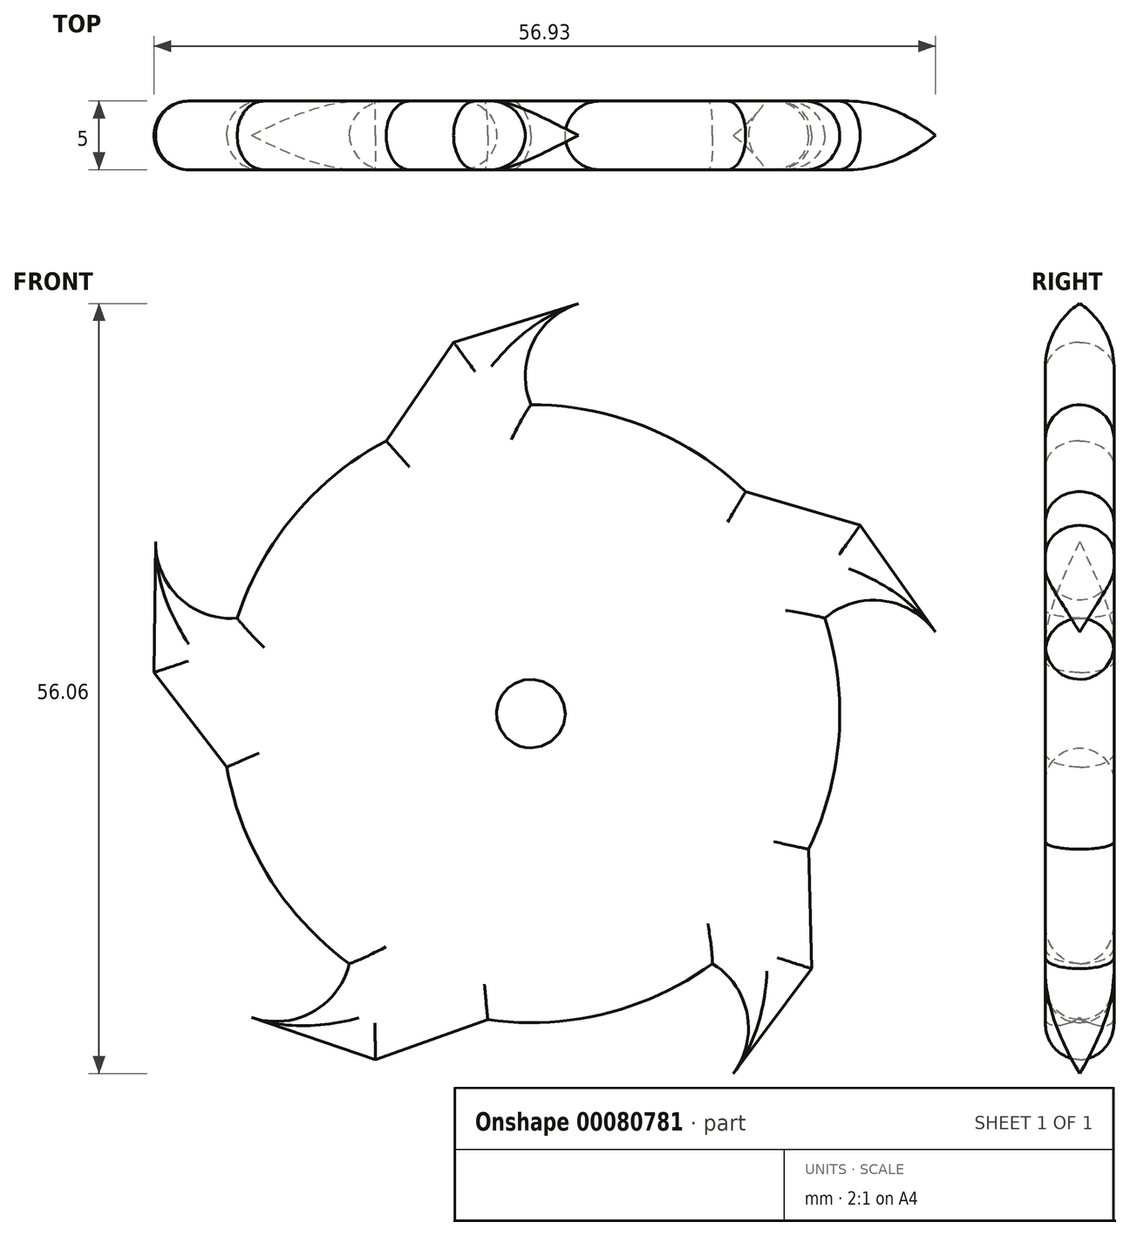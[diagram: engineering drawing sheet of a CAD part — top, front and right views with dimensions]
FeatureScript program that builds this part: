
annotation { "Feature Type Name" : "Feature", "Feature Type Description" : "" }
export const myFeature = defineFeature(function(context is Context, id is Id, definition is map)
    precondition{}
    {
        {
            var Q0;
            Q0=qCreatedBy(makeId("Front.planeOp"),FACE);
            var sketch = newSketch(context, id + "F0", { "sketchPlane" : qUnion([Q0])});
            skCircle(sketch, "E0", {"center": v(0, 0) * mm, "radius": 22.5 * mm});
            skLineSegment(sketch, "E1", {"start": v(-10.55, 19.87) * mm, "end": v(-5.64, 27.04) * mm});
            skLineSegment(sketch, "E2", {"start": v(-5.64, 27.04) * mm, "end": v(3.46, 29.86) * mm});
            skCircle(sketch, "E3", {"center": v(0, 0) * mm, "radius": 2.5 * mm});
            skArc(sketch, "E4", {"start": v(3.46, 29.86) * mm, "mid": v(0.1, 26.95) * mm, "end": v(0, 22.5) * mm});
            skLineSegment(sketch, "E5.1.0", {"start": v(-27.46, 3) * mm, "end": v(-27.33, 12.52) * mm});
            skLineSegment(sketch, "E5.1.1", {"start": v(-22.16, -3.9) * mm, "end": v(-27.46, 3) * mm});
            skArc(sketch, "E5.1.2", {"start": v(-27.33, 12.52) * mm, "mid": v(-25.6, 8.43) * mm, "end": v(-21.4, 6.95) * mm});
            skLineSegment(sketch, "E5.2.0", {"start": v(-11.34, -25.2) * mm, "end": v(-20.36, -22.13) * mm});
            skLineSegment(sketch, "E5.2.1", {"start": v(-3.14, -22.28) * mm, "end": v(-11.34, -25.2) * mm});
            skArc(sketch, "E5.2.2", {"start": v(-20.36, -22.13) * mm, "mid": v(-15.93, -21.74) * mm, "end": v(-13.23, -18.2) * mm});
            skLineSegment(sketch, "E6.1.3.0", {"start": v(20.46, -18.57) * mm, "end": v(14.75, -26.2) * mm});
            skLineSegment(sketch, "E6.3.3.0", {"start": v(20.22, -9.88) * mm, "end": v(20.46, -18.57) * mm});
            skArc(sketch, "E6.6.3.0", {"start": v(14.75, -26.2) * mm, "mid": v(15.75, -21.86) * mm, "end": v(13.23, -18.2) * mm});
            skLineSegment(sketch, "E6.1.4.0", {"start": v(23.98, 13.72) * mm, "end": v(29.47, 5.93) * mm});
            skLineSegment(sketch, "E6.3.4.0", {"start": v(15.64, 16.18) * mm, "end": v(23.98, 13.72) * mm});
            skArc(sketch, "E6.6.4.0", {"start": v(29.47, 5.93) * mm, "mid": v(25.66, 8.22) * mm, "end": v(21.4, 6.95) * mm});
            skSolve(sketch);
        }
        {
            var Q0;
            Q0=makeQuery(id+"F0.imprint","IMPRINT",FACE,{"disambiguationData":[TD([[makeQuery(id+"F0.imprint","IMPRINT",EDGE,{"derivedFrom":sQuery(id+"F0.wireOp",EDGE,"E3")}),-1.0]])]});
            var Q1;
            {var subQ0=sQuery(id+"F0.wireOp",EDGE,"E1");Q1=makeQuery(id+"F0.imprint","IMPRINT",FACE,{"disambiguationData":[TD([[makeQuery(id+"F0.imprint","IMPRINT",EDGE,{"derivedFrom":subQ0}),-1.0]])]});}
            var Q2;
            Q2=makeQuery(id+"F0.imprint","IMPRINT",FACE,{"disambiguationData":[TD([[makeQuery(id+"F0.imprint","IMPRINT",EDGE,{"derivedFrom":sQuery(id+"F0.wireOp",EDGE,"E5.1.0")}),-1.0]])]});
            var Q3;
            Q3=makeQuery(id+"F0.imprint","IMPRINT",FACE,{"disambiguationData":[TD([[makeQuery(id+"F0.imprint","IMPRINT",EDGE,{"derivedFrom":sQuery(id+"F0.wireOp",EDGE,"E5.2.0")}),-1.0]])]});
            var Q4;
            Q4=makeQuery(id+"F0.imprint","IMPRINT",FACE,{"disambiguationData":[TD([[makeQuery(id+"F0.imprint","IMPRINT",EDGE,{"derivedFrom":sQuery(id+"F0.wireOp",EDGE,"E6.1.3.0")}),-1.0]])]});
            var Q5;
            Q5=makeQuery(id+"F0.imprint","IMPRINT",FACE,{"disambiguationData":[TD([[makeQuery(id+"F0.imprint","IMPRINT",EDGE,{"derivedFrom":sQuery(id+"F0.wireOp",EDGE,"E6.1.4.0")}),-1.0]])]});
            var Q6;
            Q6=makeQuery(id+"F0.imprint","IMPRINT",FACE,{"disambiguationData":[TD([[makeQuery(id+"F0.imprint","IMPRINT",EDGE,{"derivedFrom":sQuery(id+"F0.wireOp",EDGE,"0a4afba6-e0dd-443b-8d0a-7748f586e94c.1.6.0")}),-1.0]])]});
            var Q7;
            Q7=makeQuery(id+"F0.imprint","IMPRINT",FACE,{"disambiguationData":[TD([[makeQuery(id+"F0.imprint","IMPRINT",EDGE,{"derivedFrom":sQuery(id+"F0.wireOp",EDGE,"0a4afba6-e0dd-443b-8d0a-7748f586e94c.1.5.0")}),-1.0]])]});
            extrude(context, id + "F1", {"entities" : qUnion([Q0, Q1, Q2, Q3, Q4, Q5, Q6, Q7]), "depth" : 5 * mm});
        }
        {
            var Q0;
            Q0=makeQuery(id+"F1.opExtrude","CAP_FACE",FACE,{"disambiguationData":[OSD([sQuery(id+"F0.wireOp",EDGE,"E0"),sQuery(id+"F0.wireOp",EDGE,"E1"),sQuery(id+"F0.wireOp",EDGE,"E2"),sQuery(id+"F0.wireOp",EDGE,"E3"),sQuery(id+"F0.wireOp",EDGE,"E4"),sQuery(id+"F0.wireOp",EDGE,"E5.1.0"),sQuery(id+"F0.wireOp",EDGE,"E5.1.1"),sQuery(id+"F0.wireOp",EDGE,"E5.1.2"),sQuery(id+"F0.wireOp",EDGE,"E5.2.0"),sQuery(id+"F0.wireOp",EDGE,"E5.2.1"),sQuery(id+"F0.wireOp",EDGE,"E5.2.2"),sQuery(id+"F0.wireOp",EDGE,"E6.1.3.0"),sQuery(id+"F0.wireOp",EDGE,"E6.3.3.0"),sQuery(id+"F0.wireOp",EDGE,"E6.6.3.0"),sQuery(id+"F0.wireOp",EDGE,"E6.1.4.0"),sQuery(id+"F0.wireOp",EDGE,"E6.3.4.0"),sQuery(id+"F0.wireOp",EDGE,"E6.6.4.0"),sQuery(id+"F0.wireOp",EDGE,"0a4afba6-e0dd-443b-8d0a-7748f586e94c.1.5.0"),sQuery(id+"F0.wireOp",EDGE,"0a4afba6-e0dd-443b-8d0a-7748f586e94c.3.5.0"),sQuery(id+"F0.wireOp",EDGE,"0a4afba6-e0dd-443b-8d0a-7748f586e94c.6.5.0"),sQuery(id+"F0.wireOp",EDGE,"0a4afba6-e0dd-443b-8d0a-7748f586e94c.1.6.0"),sQuery(id+"F0.wireOp",EDGE,"0a4afba6-e0dd-443b-8d0a-7748f586e94c.3.6.0"),sQuery(id+"F0.wireOp",EDGE,"0a4afba6-e0dd-443b-8d0a-7748f586e94c.6.6.0")])],"isStart":true});
            fillet(context, id + "F2", {"entities" : qUnion([Q0]), "radius" : 2.5 * mm, "tangentPropagation" : true, "allowEdgeOverflow" : false});
        }
        {
            var Q0;
            Q0=makeQuery(id+"F1.opExtrude","CAP_FACE",FACE,{"disambiguationData":[OSD([sQuery(id+"F0.wireOp",EDGE,"E0"),sQuery(id+"F0.wireOp",EDGE,"E1"),sQuery(id+"F0.wireOp",EDGE,"E2"),sQuery(id+"F0.wireOp",EDGE,"E3"),sQuery(id+"F0.wireOp",EDGE,"E4"),sQuery(id+"F0.wireOp",EDGE,"E5.1.0"),sQuery(id+"F0.wireOp",EDGE,"E5.1.1"),sQuery(id+"F0.wireOp",EDGE,"E5.1.2"),sQuery(id+"F0.wireOp",EDGE,"E5.2.0"),sQuery(id+"F0.wireOp",EDGE,"E5.2.1"),sQuery(id+"F0.wireOp",EDGE,"E5.2.2"),sQuery(id+"F0.wireOp",EDGE,"E6.1.3.0"),sQuery(id+"F0.wireOp",EDGE,"E6.3.3.0"),sQuery(id+"F0.wireOp",EDGE,"E6.6.3.0"),sQuery(id+"F0.wireOp",EDGE,"E6.1.4.0"),sQuery(id+"F0.wireOp",EDGE,"E6.3.4.0"),sQuery(id+"F0.wireOp",EDGE,"E6.6.4.0"),sQuery(id+"F0.wireOp",EDGE,"0a4afba6-e0dd-443b-8d0a-7748f586e94c.1.5.0"),sQuery(id+"F0.wireOp",EDGE,"0a4afba6-e0dd-443b-8d0a-7748f586e94c.3.5.0"),sQuery(id+"F0.wireOp",EDGE,"0a4afba6-e0dd-443b-8d0a-7748f586e94c.6.5.0"),sQuery(id+"F0.wireOp",EDGE,"0a4afba6-e0dd-443b-8d0a-7748f586e94c.1.6.0"),sQuery(id+"F0.wireOp",EDGE,"0a4afba6-e0dd-443b-8d0a-7748f586e94c.3.6.0"),sQuery(id+"F0.wireOp",EDGE,"0a4afba6-e0dd-443b-8d0a-7748f586e94c.6.6.0")])],"isStart":false});
            fillet(context, id + "F3", {"entities" : qUnion([Q0]), "radius" : 2.5 * mm, "tangentPropagation" : true, "allowEdgeOverflow" : false});
        }
    });
